# Revit family: Kohler Aleo 72275AR-4ND-CP Family
name_source: partatom
category: Plumbing Fixtures
revit_build: Autodesk Revit 2018 (Build: 20180329_1100(x64)
units: mm (PartAtom-declared; Revit-internal decimal feet)

## family parameters
Cut with Voids When Loaded = No
Host = Face
OmniClass Number = 23.45.55.17
OmniClass Title = Mixing Faucets
Part Type = Normal
Room Calculation Point = No
Round Connector Dimension = Use Diameter
Shared = No

## types (2) — shared parameters
CW Connection = Yes
Cold Water Inlet = Cold Water Inlet
Default Elevation = 914 mm
HW Connection = Yes
Height = 116 mm
Hot Water Inlet = Hot Water Inlet
Length = 48 mm
Spout Reach = 103 mm
URL = http://www.us.kohler.com
Width = 144 mm

## per-type parameters (varying)
| type | Assembly Code | Description | Finish | Manufacturer | Model | Type | Type Image |
| Kohler 72275AR-4ND-CP |  | Single Control basin mixer in polished Chrome( without drain) | Metal-Kohler-CP-Polished Chrome | Kohler | Kohler Aleo 72275AR-4ND-CP | 1 | 72275AR-4ND-CP.tif |
| G-Brushed Chrome | D2010900 | July Single-handle bathroom sink faucet | Metal-Kohler-G-Brushed Chrome | KOHLER Co. | K-16027-4-G | 2 | <None> |

## geometry (parser evidence)
native form markers: Sweep x3
no freeform markers — native parametric forms only
